# Revit family: Pump_Commercial-Effluent-Zoeller-280_Non_Automatic Series
name_source: partatom
category: Mechanical Equipment
units: mm (PartAtom-declared; Revit-internal decimal feet)

## family parameters
Always vertical = No
Cut with Voids When Loaded = No
OmniClass Number = 23.60.30.21
OmniClass Title = Pumps
Part Type = Normal
Room Calculation Point = No
Round Connector Dimension = Use Radius
Shared = Yes
Work Plane-Based = Yes

## types (2) — shared parameters
Assembly Code = D2010900
Cooling = Oil Filled
Cord Length = 180"
Cord Type = UL listed, 3-wire neoprene cord and plug (1 Ph) or 4-wire cord with no plug (3 Ph)
Default Elevation = 0"
Description = Single Seal Non-Automatic Submersible Sewage or Dewatering Pumps
Discharge Diameter = 2" or 3" NPT Female, Flanged Vertical
Discharge Height = 6 1/4"
Discharge Radius = 1"
Finish = Cast Iron-Zoeller-Powder Coated Epoxy
Height = 19 9/16"
Hertz = 60
Impeller = Cast Iron
Impeller Type = Non-clogging vortex
Installation Type = Floor Mounted
Insulation = Class B
Lead Wires Insulation = Class B
Length = 13 9/16"
Manufacturer = Zoeller
Material = Cast Iron-Zoeller-Powder Coated Epoxy
Max. Operating Temp. = 130.00 °F
Mechanical Seals = Carbon and Ceramic
Minimum Head = 60"
Motor Thermal Shutoff (Single Phase Only) = Thermal Overload Sensors With Automatic Reset.
Motor Type = Submersible
Operation = Non-Automatic
Phase = 1 or 3 Ph
Price = Prices may vary. Please consult Manufacturer Representative for most up-to-date price list.
Product Documentation Link = https://www.zoellerpumps.com
Product Page URL = https://www.zoellerpumps.com
RPM = 1725
Revised Date = 04/23/2024
Shipping Weight = 80 lbs
Solid Handling = 2" Spherical Solids
Square Ring & Gasket = Neoprene
Type = Permanent Split Capacitor or 3 Phase
Type Comments = Available in single or double seal designs.
URL = https://www.zoellerpumps.com
Voltage = 200-460
Warranty Information = 36 Months (Limited)
Waste Connection = Yes
Width = 10"

## per-type parameters (varying)
| type | Amps (Voltage Dependent) | Max. Flow at Min. Head | Maximum Head | Motor |
| 282 | 1.4-10.3 | 127 GPM @ 5' | 312" | 1/2 HP |
| 284 | 2.2-9.3 | 179 GPM @ 5' | 420" | 1 HP |

note: column(s) folded — value = type name in every type: Model

## geometry (parser evidence)
native form markers: Sweep x2
no freeform markers — native parametric forms only
